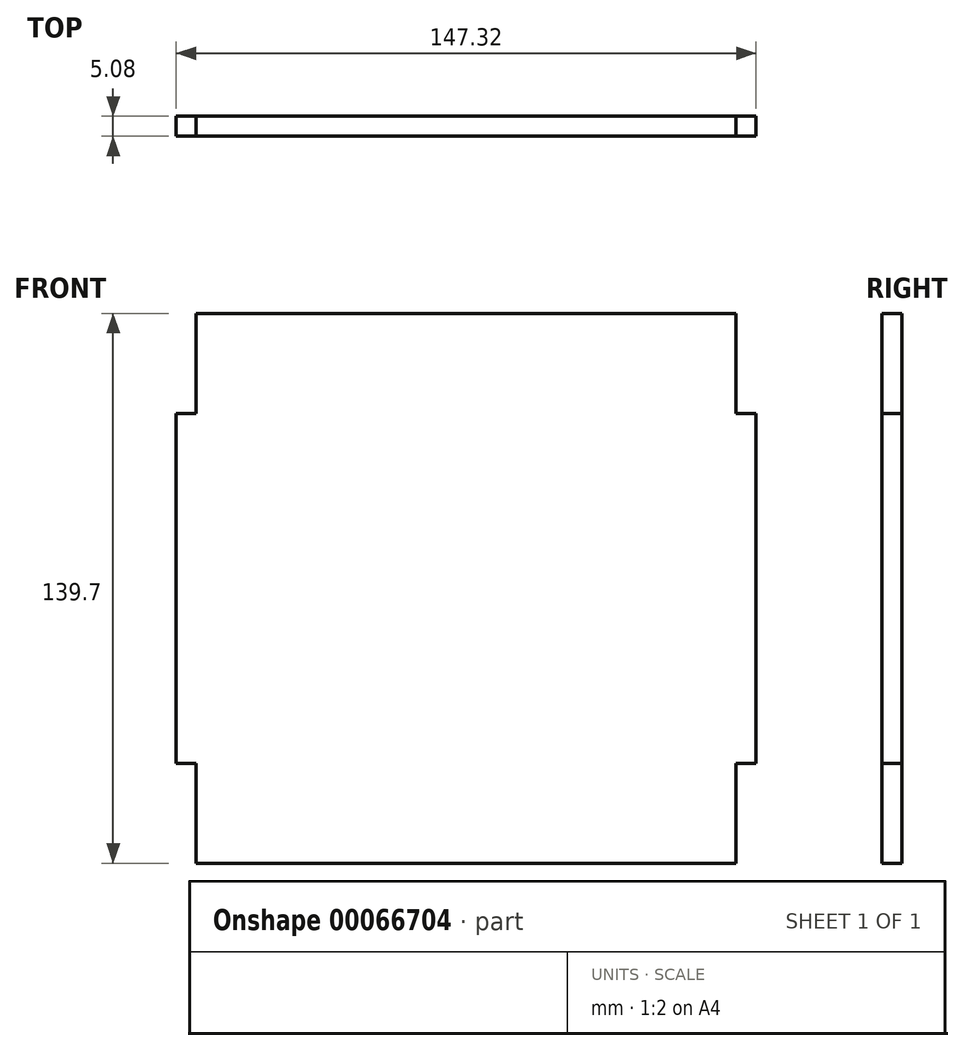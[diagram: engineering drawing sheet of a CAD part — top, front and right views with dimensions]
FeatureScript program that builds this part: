
annotation { "Feature Type Name" : "Feature", "Feature Type Description" : "" }
export const myFeature = defineFeature(function(context is Context, id is Id, definition is map)
    precondition{}
    {
        {
            var Q0;
            Q0=qCreatedBy(makeId("Front.planeOp"),FACE);
            var sketch = newSketch(context, id + "F0", { "sketchPlane" : qUnion([Q0])});
            skLineSegment(sketch, "E0.bottom", {"start": v(0, 0) * mm, "end": v(147.32, 0) * mm});
            skLineSegment(sketch, "E0.top", {"start": v(0, -139.7) * mm, "end": v(147.32, -139.7) * mm});
            skLineSegment(sketch, "E0.left", {"start": v(0, 0) * mm, "end": v(0, -139.7) * mm});
            skLineSegment(sketch, "E0.right", {"start": v(147.32, 0) * mm, "end": v(147.32, -139.7) * mm});
            skSolve(sketch);
        }
        {
            var Q0;
            Q0 = qSketchRegion(id + "F0", true);
            extrude(context, id + "F1", {"entities" : qUnion([Q0]), "depth" : 5.08 * mm});
        }
        {
            var Q0;
            Q0=makeQuery(id+"F1.opExtrude","SWEPT_FACE",FACE,{"disambiguationData":[OSD([sQuery(id+"F0.wireOp",EDGE,"E0.right")])]});
            var sketch = newSketch(context, id + "F2", { "sketchPlane" : qUnion([Q0])});
            skLineSegment(sketch, "E1.bottom", {"start": v(0, 0) * mm, "end": v(-5.08, 0) * mm});
            skLineSegment(sketch, "E1.top", {"start": v(0, -25.4) * mm, "end": v(-5.08, -25.4) * mm});
            skLineSegment(sketch, "E1.left", {"start": v(0, 0) * mm, "end": v(0, -25.4) * mm});
            skLineSegment(sketch, "E1.right", {"start": v(-5.08, 0) * mm, "end": v(-5.08, -25.4) * mm});
            skLineSegment(sketch, "E2.bottom", {"start": v(-5.08, -139.7) * mm, "end": v(0, -139.7) * mm});
            skLineSegment(sketch, "E2.top", {"start": v(-5.08, -114.3) * mm, "end": v(0, -114.3) * mm});
            skLineSegment(sketch, "E2.left", {"start": v(-5.08, -139.7) * mm, "end": v(-5.08, -114.3) * mm});
            skLineSegment(sketch, "E2.right", {"start": v(0, -139.7) * mm, "end": v(0, -114.3) * mm});
            skSolve(sketch);
        }
        {
            var Q0;
            Q0=makeQuery(id+"F1.opExtrude","SWEPT_FACE",FACE,{"disambiguationData":[OSD([sQuery(id+"F0.wireOp",EDGE,"E0.left")])]});
            var sketch = newSketch(context, id + "F3", { "sketchPlane" : qUnion([Q0])});
            skLineSegment(sketch, "E3.bottom", {"start": v(0, 0) * mm, "end": v(5.08, 0) * mm});
            skLineSegment(sketch, "E3.top", {"start": v(0, -25.4) * mm, "end": v(5.08, -25.4) * mm});
            skLineSegment(sketch, "E3.left", {"start": v(0, 0) * mm, "end": v(0, -25.4) * mm});
            skLineSegment(sketch, "E3.right", {"start": v(5.08, 0) * mm, "end": v(5.08, -25.4) * mm});
            skLineSegment(sketch, "E4.bottom", {"start": v(5.08, -139.7) * mm, "end": v(0, -139.7) * mm});
            skLineSegment(sketch, "E4.top", {"start": v(5.08, -114.3) * mm, "end": v(0, -114.3) * mm});
            skLineSegment(sketch, "E4.left", {"start": v(5.08, -139.7) * mm, "end": v(5.08, -114.3) * mm});
            skLineSegment(sketch, "E4.right", {"start": v(0, -139.7) * mm, "end": v(0, -114.3) * mm});
            skSolve(sketch);
        }
        {
            var Q0;
            Q0=makeQuery(id+"F3.imprint","IMPRINT",FACE,{"disambiguationData":[TD([[makeQuery(id+"F3.imprint","IMPRINT",EDGE,{"derivedFrom":sQuery(id+"F3.wireOp",EDGE,"E3.bottom")}),1.0]])]});
            var Q1;
            Q1=makeQuery(id+"F3.imprint","IMPRINT",FACE,{"disambiguationData":[TD([[makeQuery(id+"F3.imprint","IMPRINT",EDGE,{"derivedFrom":sQuery(id+"F3.wireOp",EDGE,"E4.bottom")}),-1.0]])]});
            var Q2;
            Q2=makeQuery(id+"F2.imprint","IMPRINT",FACE,{"disambiguationData":[TD([[makeQuery(id+"F2.imprint","IMPRINT",EDGE,{"derivedFrom":sQuery(id+"F2.wireOp",EDGE,"E1.bottom")}),-1.0]])]});
            var Q3;
            Q3=makeQuery(id+"F2.imprint","IMPRINT",FACE,{"disambiguationData":[TD([[makeQuery(id+"F2.imprint","IMPRINT",EDGE,{"derivedFrom":sQuery(id+"F2.wireOp",EDGE,"E2.bottom")}),1.0]])]});
            extrude(context, id + "F4", {"entities" : qUnion([Q0, Q1, Q2, Q3]), "operationType" : NewBodyOperationType.REMOVE, "oppositeDirection" : true, "depth" : 5.08 * mm, "hasSecondDirection" : true, "secondDirectionOppositeDirection" : false, "secondDirectionDepth" : 5.08 * mm});
        }
    });
